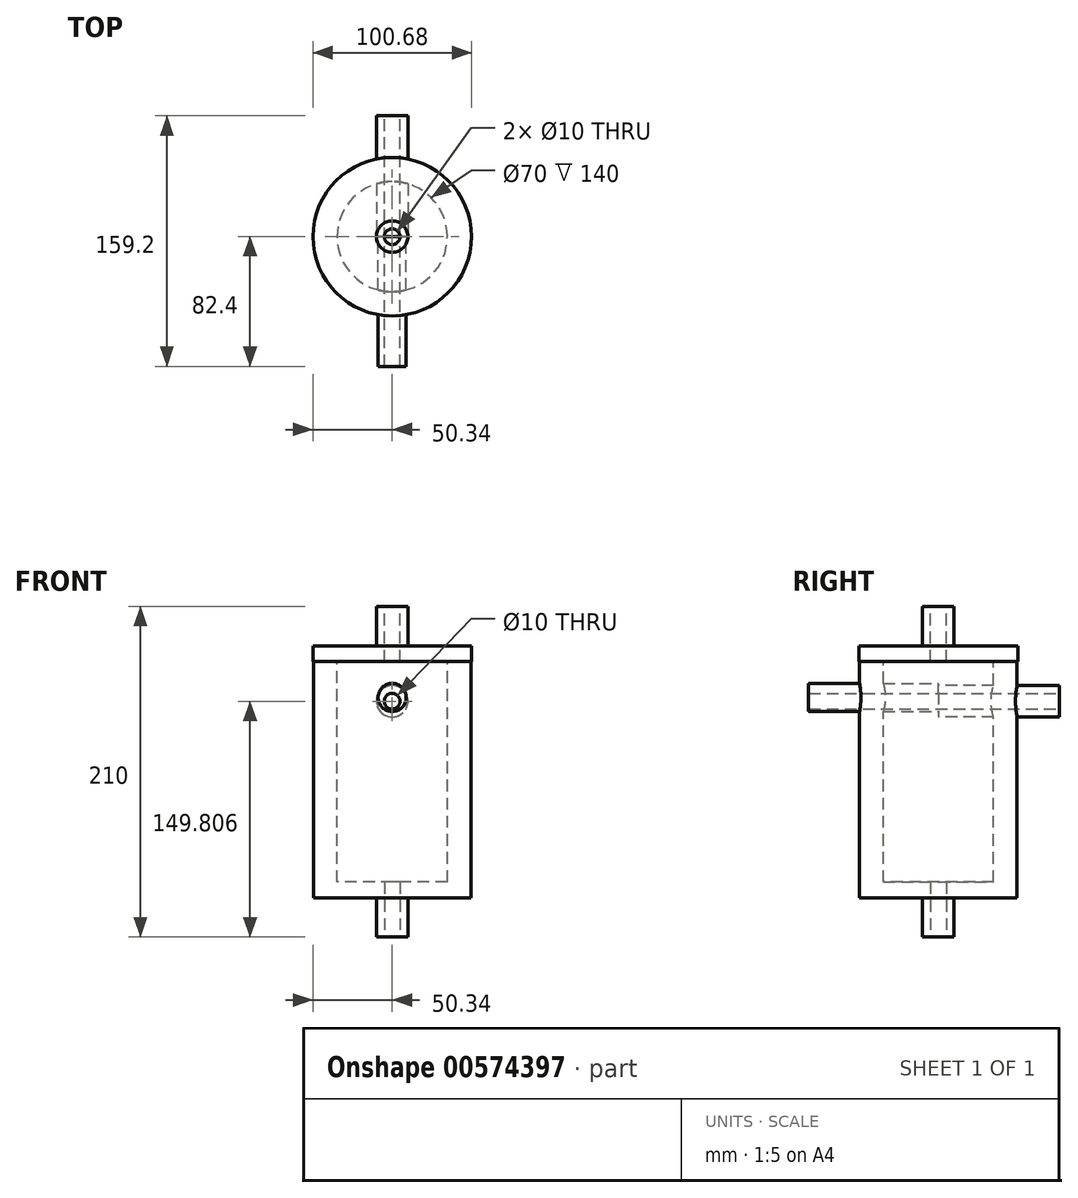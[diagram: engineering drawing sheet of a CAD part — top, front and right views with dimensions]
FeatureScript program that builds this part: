
annotation { "Feature Type Name" : "Feature", "Feature Type Description" : "" }
export const myFeature = defineFeature(function(context is Context, id is Id, definition is map)
    precondition{}
    {
        {
            var Q0;
            Q0=qCreatedBy(makeId("Top.planeOp"),FACE);
            var sketch = newSketch(context, id + "F0", { "sketchPlane" : qUnion([Q0])});
            skCircle(sketch, "E0", {"center": v(0, 0) * mm, "radius": 50 * mm});
            skSolve(sketch);
        }
        {
            var Q0;
            Q0=makeQuery(id+"F0.imprint","IMPRINT",FACE,{"disambiguationData":[TD([[makeQuery(id+"F0.imprint","IMPRINT",EDGE,{"derivedFrom":sQuery(id+"F0.wireOp",EDGE,"E0")}),1.0]])]});
            extrude(context, id + "F1", {"entities" : qUnion([Q0]), "depth" : 150 * mm, "offsetDistance" : 25 * mm});
        }
        {
            var Q0;
            Q0=makeQuery(id+"F1.opExtrude","CAP_FACE",FACE,{"disambiguationData":[OSD([sQuery(id+"F0.wireOp",EDGE,"E0")])],"isStart":false});
            var sketch = newSketch(context, id + "F2", { "sketchPlane" : qUnion([Q0])});
            skCircle(sketch, "E1", {"center": v(0, 0) * mm, "radius": 35 * mm});
            skSolve(sketch);
        }
        {
            var Q0;
            Q0=makeQuery(id+"F2.imprint","IMPRINT",FACE,{"disambiguationData":[TD([[makeQuery(id+"F2.imprint","IMPRINT",EDGE,{"derivedFrom":sQuery(id+"F2.wireOp",EDGE,"E1")}),1.0]])]});
            extrude(context, id + "F3", {"entities" : qUnion([Q0]), "operationType" : NewBodyOperationType.REMOVE, "oppositeDirection" : true, "depth" : 140 * mm, "offsetDistance" : 25 * mm});
        }
        {
            var Q0;
            Q0=makeQuery(id+"F1.opExtrude","CAP_FACE",FACE,{"disambiguationData":[OSD([sQuery(id+"F0.wireOp",EDGE,"E0")])],"isStart":true});
            var sketch = newSketch(context, id + "F4", { "sketchPlane" : qUnion([Q0])});
            skCircle(sketch, "E2", {"center": v(0, 0) * mm, "radius": 10 * mm});
            skSolve(sketch);
        }
        {
            var Q0;
            Q0=makeQuery(id+"F4.imprint","IMPRINT",FACE,{"disambiguationData":[TD([[makeQuery(id+"F4.imprint","IMPRINT",EDGE,{"derivedFrom":sQuery(id+"F4.wireOp",EDGE,"E2")}),1.0]])]});
            extrude(context, id + "F5", {"entities" : qUnion([Q0]), "operationType" : NewBodyOperationType.ADD, "depth" : 25 * mm, "offsetDistance" : 25 * mm});
        }
        {
            var Q0;
            Q0=qCreatedBy(makeId("Front.planeOp"),FACE);
            var sketch = newSketch(context, id + "F6", { "sketchPlane" : qUnion([Q0])});
            skCircle(sketch, "E3", {"center": v(0, 127.22) * mm, "radius": 8.9 * mm});
            skSolve(sketch);
        }
        {
            var Q0;
            Q0 = qSketchRegion(id + "F6", true);
            extrude(context, id + "F7", {"entities" : qUnion([Q0]), "depth" : 82.4 * mm, "offsetDistance" : 25 * mm});
        }
        {
            var Q0;
            Q0=qCreatedBy(makeId("Front.planeOp"),FACE);
            var sketch = newSketch(context, id + "F8", { "sketchPlane" : qUnion([Q0])});
            skCircle(sketch, "E4", {"center": v(0, 124.8) * mm, "radius": 10 * mm});
            skSolve(sketch);
        }
        {
            var Q0;
            Q0 = qSketchRegion(id + "F8", true);
            extrude(context, id + "F9", {"entities" : qUnion([Q0]), "operationType" : NewBodyOperationType.ADD, "oppositeDirection" : true, "depth" : 76.8 * mm, "offsetDistance" : 25 * mm});
        }
        {
            var Q0;
            Q0=makeQuery(id+"F5.opExtrude","CAP_FACE",FACE,{"disambiguationData":[OSD([sQuery(id+"F4.wireOp",EDGE,"E2")])],"isStart":false});
            var sketch = newSketch(context, id + "F10", { "sketchPlane" : qUnion([Q0])});
            skCircle(sketch, "E5", {"center": v(0, 0) * mm, "radius": 5 * mm});
            skSolve(sketch);
        }
        {
            var Q0;
            Q0=makeQuery(id+"F10.imprint","IMPRINT",FACE,{"disambiguationData":[TD([[makeQuery(id+"F10.imprint","IMPRINT",EDGE,{"derivedFrom":sQuery(id+"F10.wireOp",EDGE,"E5")}),1.0]])]});
            extrude(context, id + "F11", {"entities" : qUnion([Q0]), "operationType" : NewBodyOperationType.REMOVE, "oppositeDirection" : true, "depth" : 50 * mm, "offsetDistance" : 25 * mm});
        }
        {
            var Q0;
            Q0=makeQuery(id+"F9.opExtrude","CAP_FACE",FACE,{"disambiguationData":[OSD([sQuery(id+"F8.wireOp",EDGE,"E4")])],"isStart":false});
            var sketch = newSketch(context, id + "F12", { "sketchPlane" : qUnion([Q0])});
            skCircle(sketch, "E6", {"center": v(0, 124.8) * mm, "radius": 5 * mm});
            skSolve(sketch);
        }
        {
            var Q0;
            Q0=makeQuery(id+"F12.imprint","IMPRINT",FACE,{"disambiguationData":[TD([[makeQuery(id+"F12.imprint","IMPRINT",EDGE,{"derivedFrom":sQuery(id+"F12.wireOp",EDGE,"E6")}),1.0]])]});
            extrude(context, id + "F13", {"entities" : qUnion([Q0]), "operationType" : NewBodyOperationType.REMOVE, "oppositeDirection" : true, "depth" : 200 * mm, "offsetDistance" : 25 * mm});
        }
        {
            var Q0;
            Q0=makeQuery(id+"F1.opExtrude","CAP_FACE",FACE,{"disambiguationData":[OSD([sQuery(id+"F0.wireOp",EDGE,"E0")])],"isStart":false});
            var sketch = newSketch(context, id + "F14", { "sketchPlane" : qUnion([Q0])});
            skCircle(sketch, "E7", {"center": v(0, 0) * mm, "radius": 50.34 * mm});
            skSolve(sketch);
        }
        {
            var Q0;
            Q0 = qSketchRegion(id + "F14", true);
            extrude(context, id + "F15", {"entities" : qUnion([Q0]), "operationType" : NewBodyOperationType.ADD, "depth" : 10 * mm, "offsetDistance" : 25 * mm});
        }
        {
            var Q0;
            Q0=makeQuery(id+"F15.opExtrude","CAP_FACE",FACE,{"disambiguationData":[OSD([sQuery(id+"F14.wireOp",EDGE,"E7")])],"isStart":false});
            var sketch = newSketch(context, id + "F16", { "sketchPlane" : qUnion([Q0])});
            skCircle(sketch, "E8", {"center": v(0, 0) * mm, "radius": 10 * mm});
            skSolve(sketch);
        }
        {
            var Q0;
            Q0=makeQuery(id+"F16.imprint","IMPRINT",FACE,{"disambiguationData":[TD([[makeQuery(id+"F16.imprint","IMPRINT",EDGE,{"derivedFrom":sQuery(id+"F16.wireOp",EDGE,"E8")}),1.0]])]});
            extrude(context, id + "F17", {"entities" : qUnion([Q0]), "operationType" : NewBodyOperationType.ADD, "depth" : 25 * mm, "offsetDistance" : 25 * mm});
        }
        {
            var Q0;
            Q0=makeQuery(id+"F17.opExtrude","CAP_FACE",FACE,{"disambiguationData":[OSD([sQuery(id+"F16.wireOp",EDGE,"E8")])],"isStart":false});
            var sketch = newSketch(context, id + "F18", { "sketchPlane" : qUnion([Q0])});
            skCircle(sketch, "E9", {"center": v(0, 0) * mm, "radius": 5 * mm});
            skSolve(sketch);
        }
        {
            var Q0;
            Q0=makeQuery(id+"F18.imprint","IMPRINT",FACE,{"disambiguationData":[TD([[makeQuery(id+"F18.imprint","IMPRINT",EDGE,{"derivedFrom":sQuery(id+"F18.wireOp",EDGE,"E9")}),1.0]])]});
            extrude(context, id + "F19", {"entities" : qUnion([Q0]), "operationType" : NewBodyOperationType.REMOVE, "oppositeDirection" : true, "depth" : 40 * mm, "offsetDistance" : 25 * mm});
        }
    });
